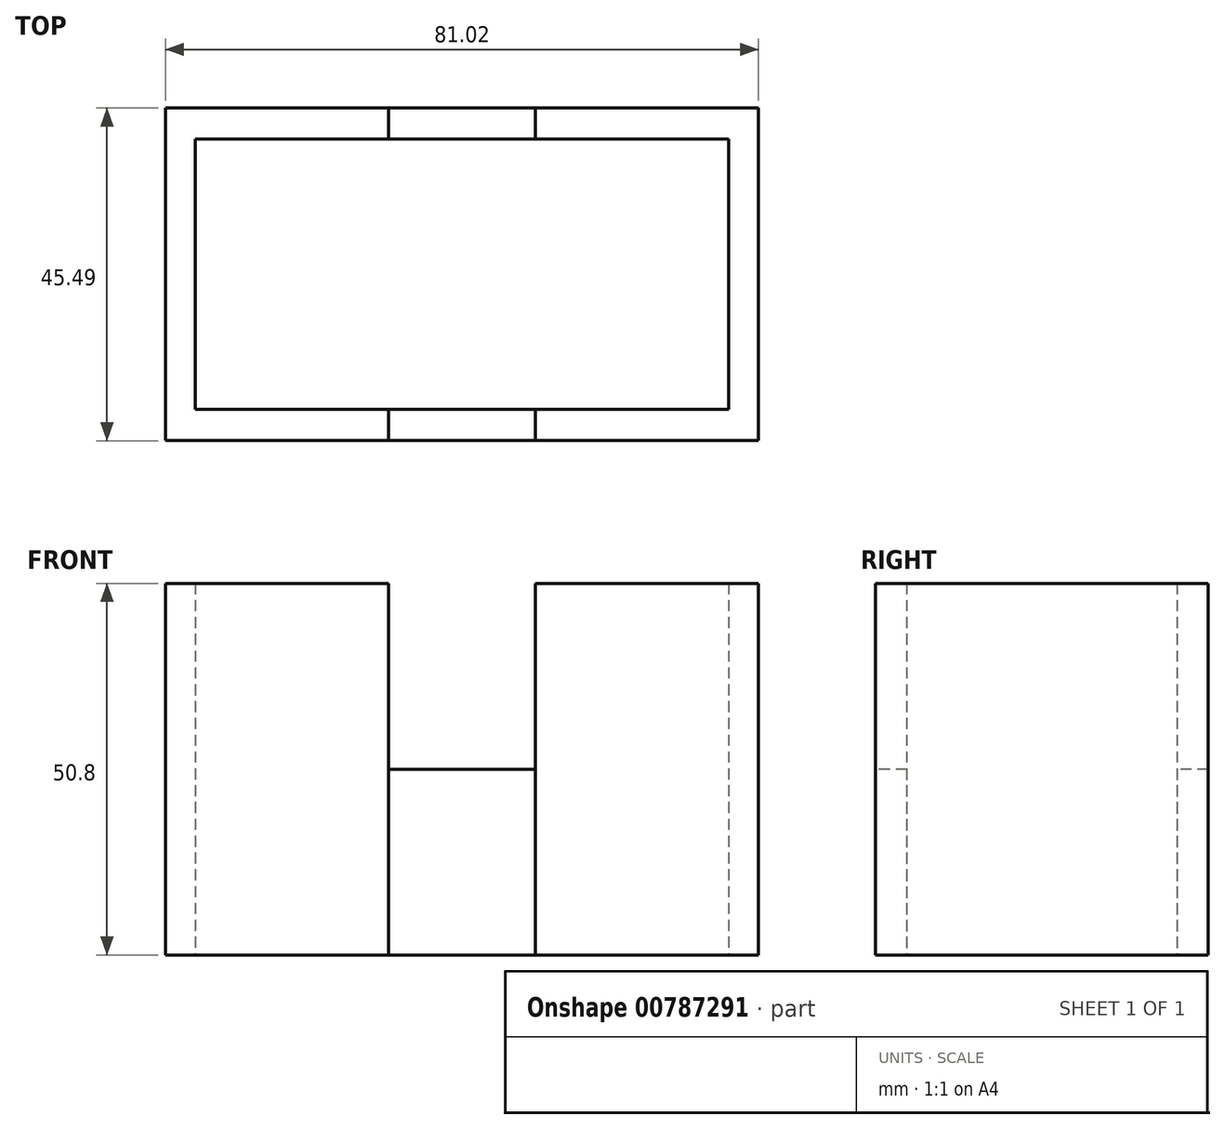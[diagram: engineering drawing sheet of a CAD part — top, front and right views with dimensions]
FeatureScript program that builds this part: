
annotation { "Feature Type Name" : "Feature", "Feature Type Description" : "" }
export const myFeature = defineFeature(function(context is Context, id is Id, definition is map)
    precondition{}
    {
        {
            var Q0;
            Q0=qCreatedBy(makeId("Top.planeOp"),FACE);
            var sketch = newSketch(context, id + "F0", { "sketchPlane" : qUnion([Q0])});
            skLineSegment(sketch, "E0", {"start": v(-40.51, 29.75) * mm, "end": v(-40.51, -15.74) * mm});
            skLineSegment(sketch, "E1", {"start": v(-40.51, -15.74) * mm, "end": v(-36.45, -15.74) * mm});
            skLineSegment(sketch, "E2", {"start": v(-36.45, -11.47) * mm, "end": v(-36.45, 25.49) * mm});
            skLineSegment(sketch, "E3", {"start": v(-36.45, 29.75) * mm, "end": v(-40.51, 29.75) * mm});
            skLineSegment(sketch, "E4", {"start": v(-36.45, -11.47) * mm, "end": v(-10.05, -11.47) * mm});
            skLineSegment(sketch, "E5", {"start": v(-10.05, -11.47) * mm, "end": v(-10.05, -15.74) * mm});
            skLineSegment(sketch, "E6", {"start": v(-10.05, -15.74) * mm, "end": v(-36.45, -15.74) * mm});
            skLineSegment(sketch, "E7", {"start": v(-36.45, 29.75) * mm, "end": v(-10.05, 29.75) * mm});
            skLineSegment(sketch, "E8", {"start": v(-10.05, 29.75) * mm, "end": v(-10.05, 25.49) * mm});
            skLineSegment(sketch, "E9", {"start": v(-10.05, 25.49) * mm, "end": v(-36.45, 25.49) * mm});
            skLineSegment(sketch, "E10.MirrorCS", {"start": v(36.45, 29.75) * mm, "end": v(10.05, 29.75) * mm});
            skLineSegment(sketch, "E11.MirrorCS", {"start": v(10.05, 25.49) * mm, "end": v(36.45, 25.49) * mm});
            skLineSegment(sketch, "E12.MirrorCS", {"start": v(10.05, 29.75) * mm, "end": v(10.05, 25.49) * mm});
            skLineSegment(sketch, "E13.MirrorCS", {"start": v(36.45, 29.75) * mm, "end": v(40.51, 29.75) * mm});
            skLineSegment(sketch, "E14.MirrorCS", {"start": v(40.51, 29.75) * mm, "end": v(40.51, -15.74) * mm});
            skLineSegment(sketch, "E15.MirrorCS", {"start": v(36.45, -11.47) * mm, "end": v(36.45, 25.49) * mm});
            skLineSegment(sketch, "E16.MirrorCS", {"start": v(36.45, -11.47) * mm, "end": v(10.05, -11.47) * mm});
            skLineSegment(sketch, "E17.MirrorCS", {"start": v(10.05, -15.74) * mm, "end": v(36.45, -15.74) * mm});
            skLineSegment(sketch, "E18.MirrorCS", {"start": v(10.05, -11.47) * mm, "end": v(10.05, -15.74) * mm});
            skLineSegment(sketch, "E19.MirrorCS", {"start": v(40.51, -15.74) * mm, "end": v(36.45, -15.74) * mm});
            skLineSegment(sketch, "E20", {"start": v(-10.05, 29.75) * mm, "end": v(10.05, 29.75) * mm});
            skLineSegment(sketch, "E21", {"start": v(10.05, 25.49) * mm, "end": v(-10.05, 25.49) * mm});
            skLineSegment(sketch, "E22", {"start": v(-10.05, -11.47) * mm, "end": v(10.05, -11.47) * mm});
            skLineSegment(sketch, "E23", {"start": v(10.05, -15.74) * mm, "end": v(-10.05, -15.74) * mm});
            skSolve(sketch);
        }
        {
            var Q0;
            Q0=makeQuery(id+"F0.imprint","IMPRINT",FACE,{"disambiguationData":[TD([[makeQuery(id+"F0.imprint","IMPRINT",EDGE,{"derivedFrom":sQuery(id+"F0.wireOp",EDGE,"E0")}),1.0]])]});
            var Q1;
            Q1=makeQuery(id+"F0.imprint","IMPRINT",FACE,{"disambiguationData":[TD([[makeQuery(id+"F0.imprint","IMPRINT",EDGE,{"derivedFrom":sQuery(id+"F0.wireOp",EDGE,"E10.MirrorCS")}),1.0]])]});
            extrude(context, id + "F1", {"entities" : qUnion([Q0, Q1]), "depth" : 50.8 * mm, "offsetDistance" : 25.4 * mm});
        }
        {
            var Q0;
            Q0=makeQuery(id+"F0.imprint","IMPRINT",FACE,{"disambiguationData":[TD([[makeQuery(id+"F0.imprint","IMPRINT",EDGE,{"derivedFrom":sQuery(id+"F0.wireOp",EDGE,"E8")}),1.0]])]});
            var Q1;
            Q1=makeQuery(id+"F0.imprint","IMPRINT",FACE,{"disambiguationData":[TD([[makeQuery(id+"F0.imprint","IMPRINT",EDGE,{"derivedFrom":sQuery(id+"F0.wireOp",EDGE,"E5")}),1.0]])]});
            extrude(context, id + "F2", {"entities" : qUnion([Q0, Q1]), "depth" : 25.4 * mm, "offsetDistance" : 25.4 * mm});
        }
    });
